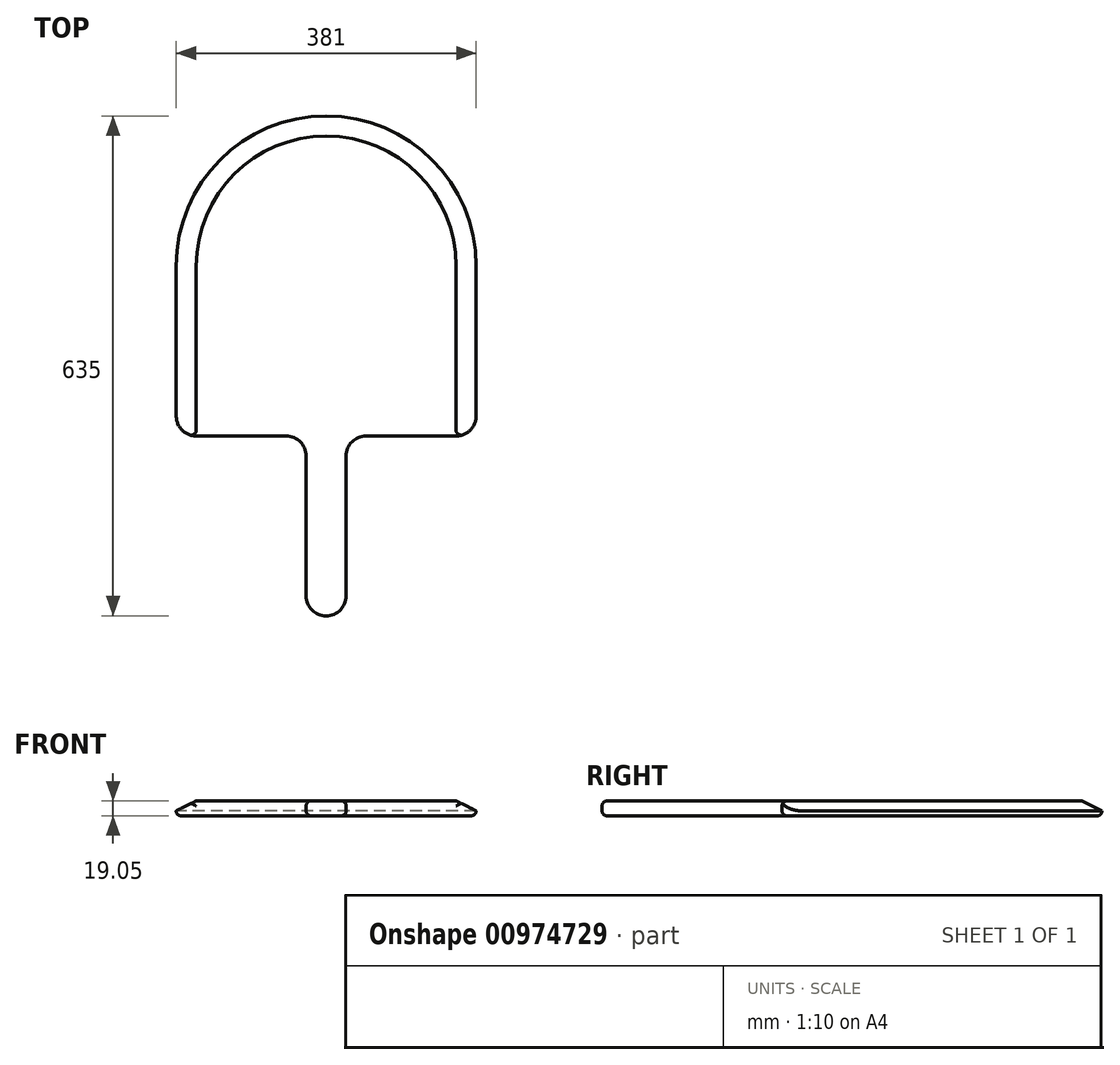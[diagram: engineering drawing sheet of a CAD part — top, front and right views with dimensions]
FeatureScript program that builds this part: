
annotation { "Feature Type Name" : "Feature", "Feature Type Description" : "" }
export const myFeature = defineFeature(function(context is Context, id is Id, definition is map)
    precondition{}
    {
        {
            var Q0;
            Q0=qCreatedBy(makeId("Top.planeOp"),FACE);
            var sketch = newSketch(context, id + "F0", { "sketchPlane" : qUnion([Q0])});
            skArc(sketch, "E0", {"start": v(190.5, 0) * mm, "mid": v(0, 190.5) * mm, "end": v(-190.5, 0) * mm});
            skLineSegment(sketch, "E1", {"start": v(-190.5, 0) * mm, "end": v(-190.5, -190.5) * mm});
            skLineSegment(sketch, "E2", {"start": v(190.5, 0) * mm, "end": v(190.5, -190.5) * mm});
            skLineSegment(sketch, "E3", {"start": v(-165.1, -215.9) * mm, "end": v(-50.8, -215.9) * mm});
            skLineSegment(sketch, "E4", {"start": v(-25.4, -241.3) * mm, "end": v(-25.4, -419.1) * mm});
            skLineSegment(sketch, "E5", {"start": v(25.4, -419.1) * mm, "end": v(25.4, -241.3) * mm});
            skLineSegment(sketch, "E6", {"start": v(50.8, -215.9) * mm, "end": v(165.1, -215.9) * mm});
            skArc(sketch, "E7", {"start": v(-190.5, -190.5) * mm, "mid": v(-183.06, -208.46) * mm, "end": v(-165.1, -215.9) * mm});
            skArc(sketch, "E8", {"start": v(165.1, -215.9) * mm, "mid": v(183.06, -208.46) * mm, "end": v(190.5, -190.5) * mm});
            skArc(sketch, "E9", {"start": v(50.8, -215.9) * mm, "mid": v(32.84, -223.34) * mm, "end": v(25.4, -241.3) * mm});
            skArc(sketch, "E10", {"start": v(-25.4, -241.3) * mm, "mid": v(-32.84, -223.34) * mm, "end": v(-50.8, -215.9) * mm});
            skArc(sketch, "E11", {"start": v(-25.4, -419.1) * mm, "mid": v(0, -444.5) * mm, "end": v(25.4, -419.1) * mm});
            skPoint(sketch, "E12.orphan", {"position": v(-190.5, -215.9) * mm});
            skPoint(sketch, "E13.orphan", {"position": v(190.5, -215.9) * mm});
            skPoint(sketch, "E14.orphan", {"position": v(25.4, -215.9) * mm});
            skSolve(sketch);
        }
        {
            var Q0;
            Q0=makeQuery(id+"F0.imprint","IMPRINT",FACE,{"disambiguationData":[TD([[makeQuery(id+"F0.imprint","IMPRINT",EDGE,{"derivedFrom":sQuery(id+"F0.wireOp",EDGE,"E0")}),1.0]])]});
            extrude(context, id + "F1", {"entities" : qUnion([Q0]), "depth" : 19.05 * mm, "offsetDistance" : 25.4 * mm});
        }
        {
            var Q0;
            Q0=makeQuery(id+"F1.opExtrude","CAP_EDGE",EDGE,{"disambiguationData":[OSD([sQuery(id+"F0.wireOp",EDGE,"E1")])],"isStart":false});
            var Q1;
            Q1=makeQuery(id+"F1.opExtrude","CAP_EDGE",EDGE,{"disambiguationData":[OSD([sQuery(id+"F0.wireOp",EDGE,"E0")])],"isStart":false});
            var Q2;
            Q2=makeQuery(id+"F1.opExtrude","CAP_EDGE",EDGE,{"disambiguationData":[OSD([sQuery(id+"F0.wireOp",EDGE,"E2")])],"isStart":false});
            chamfer(context, id + "F2", {"entities" : qUnion([Q0, Q1, Q2]), "chamferType" : ChamferType.TWO_OFFSETS, "width1" : 12.7 * mm, "oppositeDirection" : true, "width2" : 25.4 * mm});
        }
        {
            var Q0;
            Q0=makeQuery(id+"F1.opExtrude","CAP_EDGE",EDGE,{"disambiguationData":[OSD([sQuery(id+"F0.wireOp",EDGE,"E11")])],"isStart":false});
            fillet(context, id + "F3", {"entities" : qUnion([Q0]), "radius" : 6.35 * mm, "tangentPropagation" : true, "allowEdgeOverflow" : false});
        }
        {
            var Q0;
            Q0=makeQuery(id+"F1.opExtrude","CAP_FACE",FACE,{"disambiguationData":[OSD([sQuery(id+"F0.wireOp",EDGE,"E0"),sQuery(id+"F0.wireOp",EDGE,"E1"),sQuery(id+"F0.wireOp",EDGE,"E2"),sQuery(id+"F0.wireOp",EDGE,"E3"),sQuery(id+"F0.wireOp",EDGE,"E4"),sQuery(id+"F0.wireOp",EDGE,"E5"),sQuery(id+"F0.wireOp",EDGE,"E6"),sQuery(id+"F0.wireOp",EDGE,"E7"),sQuery(id+"F0.wireOp",EDGE,"E8"),sQuery(id+"F0.wireOp",EDGE,"E9"),sQuery(id+"F0.wireOp",EDGE,"E10"),sQuery(id+"F0.wireOp",EDGE,"E11")])],"isStart":true});
            fillet(context, id + "F4", {"entities" : qUnion([Q0]), "radius" : 6.35 * mm, "tangentPropagation" : true, "allowEdgeOverflow" : false});
        }
    });
